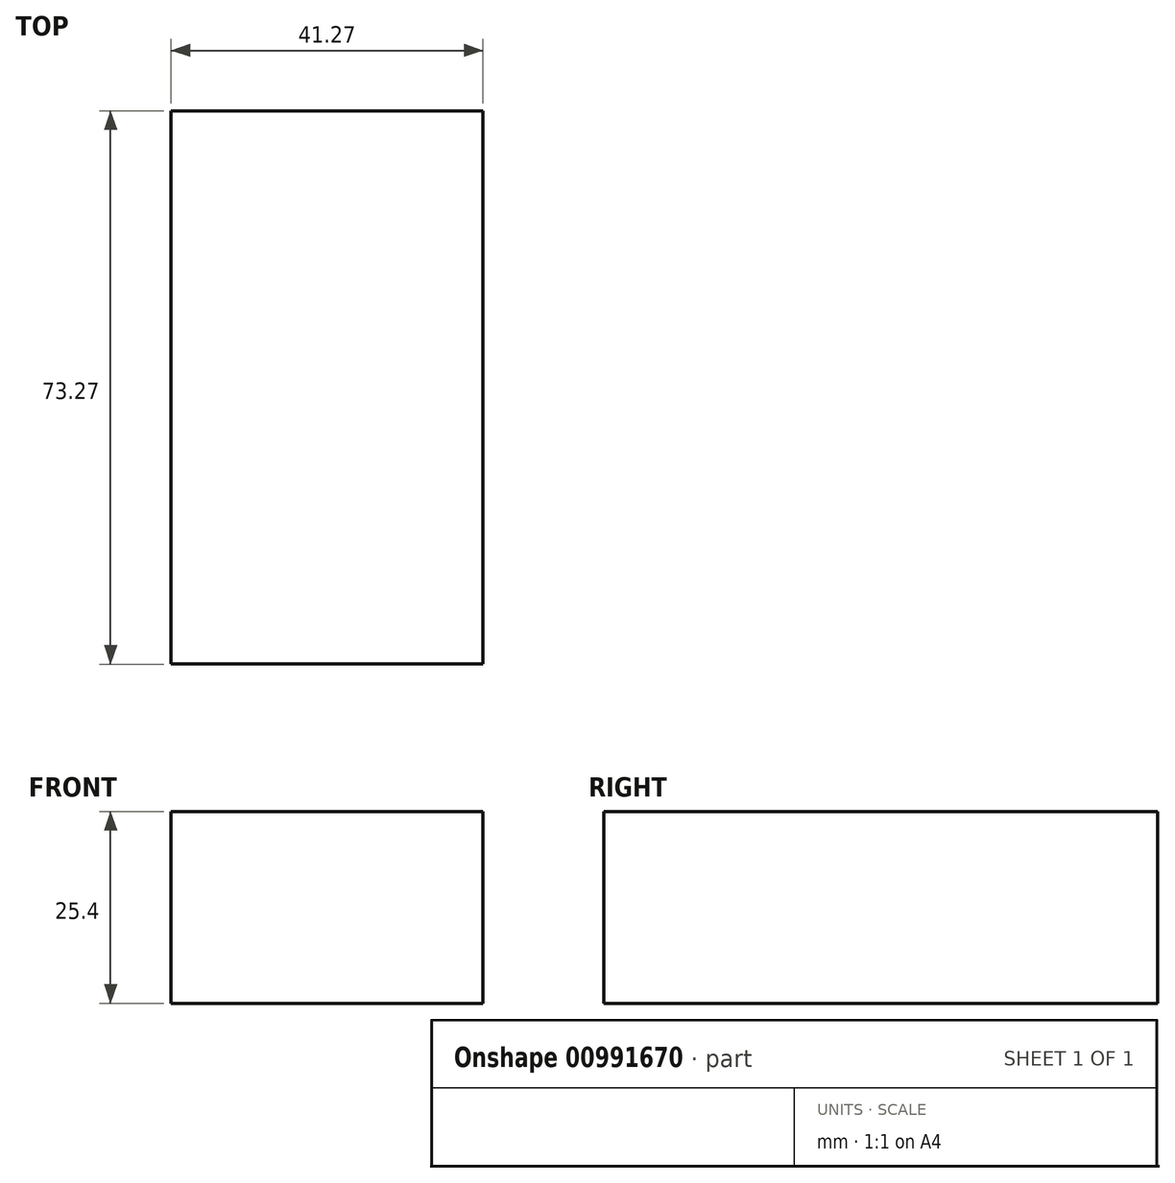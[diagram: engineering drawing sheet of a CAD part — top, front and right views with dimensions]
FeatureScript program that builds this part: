
annotation { "Feature Type Name" : "Feature", "Feature Type Description" : "" }
export const myFeature = defineFeature(function(context is Context, id is Id, definition is map)
    precondition{}
    {
        {
            var Q0;
            Q0=qCreatedBy(makeId("Top.planeOp"),FACE);
            var sketch = newSketch(context, id + "F0", { "sketchPlane" : qUnion([Q0])});
            skLineSegment(sketch, "E0.bottom", {"start": v(-19.66, 32.63) * mm, "end": v(21.61, 32.63) * mm});
            skLineSegment(sketch, "E0.top", {"start": v(-19.66, -40.64) * mm, "end": v(21.61, -40.64) * mm});
            skLineSegment(sketch, "E0.left", {"start": v(-19.66, 32.63) * mm, "end": v(-19.66, -40.64) * mm});
            skLineSegment(sketch, "E0.right", {"start": v(21.61, 32.63) * mm, "end": v(21.61, -40.64) * mm});
            skSolve(sketch);
        }
        {
            var Q0;
            Q0=makeQuery(id+"F0.imprint","IMPRINT",FACE,{"disambiguationData":[TD([[makeQuery(id+"F0.imprint","IMPRINT",EDGE,{"derivedFrom":sQuery(id+"F0.wireOp",EDGE,"E0.bottom")}),-1.0]])]});
            extrude(context, id + "F1", {"entities" : qUnion([Q0]), "depth" : 25.4 * mm, "offsetDistance" : 25.4 * mm});
        }
    });
